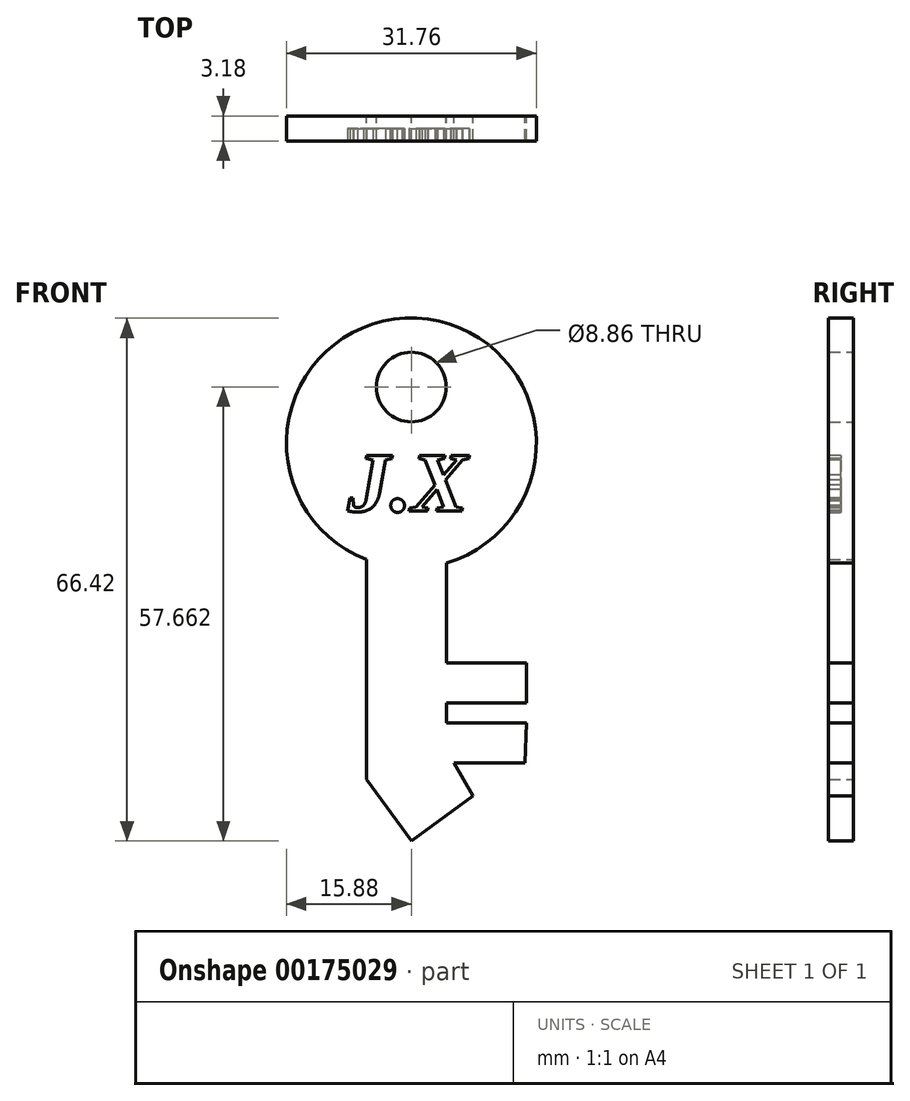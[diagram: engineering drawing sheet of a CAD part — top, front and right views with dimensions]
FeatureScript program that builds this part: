
annotation { "Feature Type Name" : "Feature", "Feature Type Description" : "" }
export const myFeature = defineFeature(function(context is Context, id is Id, definition is map)
    precondition{}
    {
        {
            var Q0;
            Q0=qCreatedBy(makeId("Front.planeOp"),FACE);
            var sketch = newSketch(context, id + "F0", { "sketchPlane" : qUnion([Q0])});
            skCircle(sketch, "E0", {"center": v(0, 29.07) * mm, "radius": 15.88 * mm});
            skLineSegment(sketch, "E1", {"start": v(-5.7, 14.25) * mm, "end": v(-5.7, -13.69) * mm});
            skLineSegment(sketch, "E2", {"start": v(-5.7, -13.69) * mm, "end": v(0, -21.48) * mm});
            skLineSegment(sketch, "E3", {"start": v(0, -21.48) * mm, "end": v(7.85, -15.73) * mm});
            skLineSegment(sketch, "E4", {"start": v(7.85, -15.73) * mm, "end": v(5.4, -11.57) * mm});
            skLineSegment(sketch, "E5", {"start": v(5.4, -11.57) * mm, "end": v(14.44, -11.57) * mm});
            skLineSegment(sketch, "E6", {"start": v(14.44, -11.57) * mm, "end": v(14.62, -6.49) * mm});
            skLineSegment(sketch, "E7", {"start": v(14.62, -6.49) * mm, "end": v(4.46, -6.49) * mm});
            skLineSegment(sketch, "E8", {"start": v(4.46, -6.49) * mm, "end": v(4.46, -3.95) * mm});
            skLineSegment(sketch, "E9", {"start": v(4.46, -3.95) * mm, "end": v(14.62, -3.95) * mm});
            skLineSegment(sketch, "E10", {"start": v(14.62, -3.95) * mm, "end": v(14.62, 1.13) * mm});
            skLineSegment(sketch, "E11", {"start": v(14.62, 1.13) * mm, "end": v(4.46, 1.13) * mm});
            skLineSegment(sketch, "E12", {"start": v(4.46, 1.13) * mm, "end": v(4.46, 13.83) * mm});
            skSolve(sketch);
        }
        {
            var Q0;
            Q0 = qSketchRegion(id + "F0", true);
            extrude(context, id + "F1", {"entities" : qUnion([Q0]), "depth" : 3.17 * mm});
        }
        {
            var Q0;
            Q0=qCreatedBy(makeId("Front.planeOp"),FACE);
            var sketch = newSketch(context, id + "F2", { "sketchPlane" : qUnion([Q0])});
            skCircle(sketch, "E13", {"center": v(0, 36.18) * mm, "radius": 4.43 * mm});
            skSolve(sketch);
        }
        {
            var Q0;
            Q0 = qSketchRegion(id + "F2", true);
            extrude(context, id + "F3", {"entities" : qUnion([Q0]), "operationType" : NewBodyOperationType.REMOVE, "depth" : 25.4 * mm});
        }
        {
            var Q0;
            Q0=makeQuery(id+"F1.opExtrude","CAP_FACE",FACE,{"disambiguationData":[OSD([sQuery(id+"F0.wireOp",EDGE,"E0"),sQuery(id+"F0.wireOp",EDGE,"E1"),sQuery(id+"F0.wireOp",EDGE,"E2"),sQuery(id+"F0.wireOp",EDGE,"E3"),sQuery(id+"F0.wireOp",EDGE,"E4"),sQuery(id+"F0.wireOp",EDGE,"E5"),sQuery(id+"F0.wireOp",EDGE,"E6"),sQuery(id+"F0.wireOp",EDGE,"E7"),sQuery(id+"F0.wireOp",EDGE,"E8"),sQuery(id+"F0.wireOp",EDGE,"E9"),sQuery(id+"F0.wireOp",EDGE,"E10"),sQuery(id+"F0.wireOp",EDGE,"E11"),sQuery(id+"F0.wireOp",EDGE,"E12")])],"isStart":false});
            var sketch = newSketch(context, id + "F4", { "sketchPlane" : qUnion([Q0])});
            skText(sketch, "E14", { "text": "J.X", "fontName": "Tinos-BoldItalic.ttf"});
            const initialGuessF4  = {"E14": [-0.00808, 0.02041, 1, 0, 0.00775]};
            skSetInitialGuess(sketch, initialGuessF4);
            skSolve(sketch);
        }
        {
            var Q0;
            Q0 = qSketchRegion(id + "F4", true);
            extrude(context, id + "F5", {"entities" : qUnion([Q0]), "operationType" : NewBodyOperationType.REMOVE, "oppositeDirection" : true, "depth" : 1.59 * mm});
        }
    });
